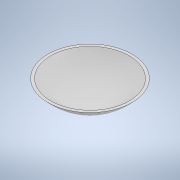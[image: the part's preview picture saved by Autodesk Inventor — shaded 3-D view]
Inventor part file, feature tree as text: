
AUTODESK INVENTOR PART (.ipt)
format: ipt  version: 2022 (Build 260153000, 153)  size: 115,712 bytes
history: native  units: mm
features: revolve x1, sketch x1
ambient origin geometry x8: Origin, YZ Plane, XZ Plane, XY Plane, X Axis, Y Axis, Z Axis, Center Point
bodies: Body1 (feature_tree)
feature tree (2):
  revolve  "Revolution1"  [1 undecoded]
  sketch  "Sketch2"  dims[d3=50.0mm d4=48.0mm d5=90.0deg]
note: 1 required parameter value undecoded (feature->parameter linkage not recoverable at this tier; creation-order binding heuristic only, values carry confidence <= 0.55)
